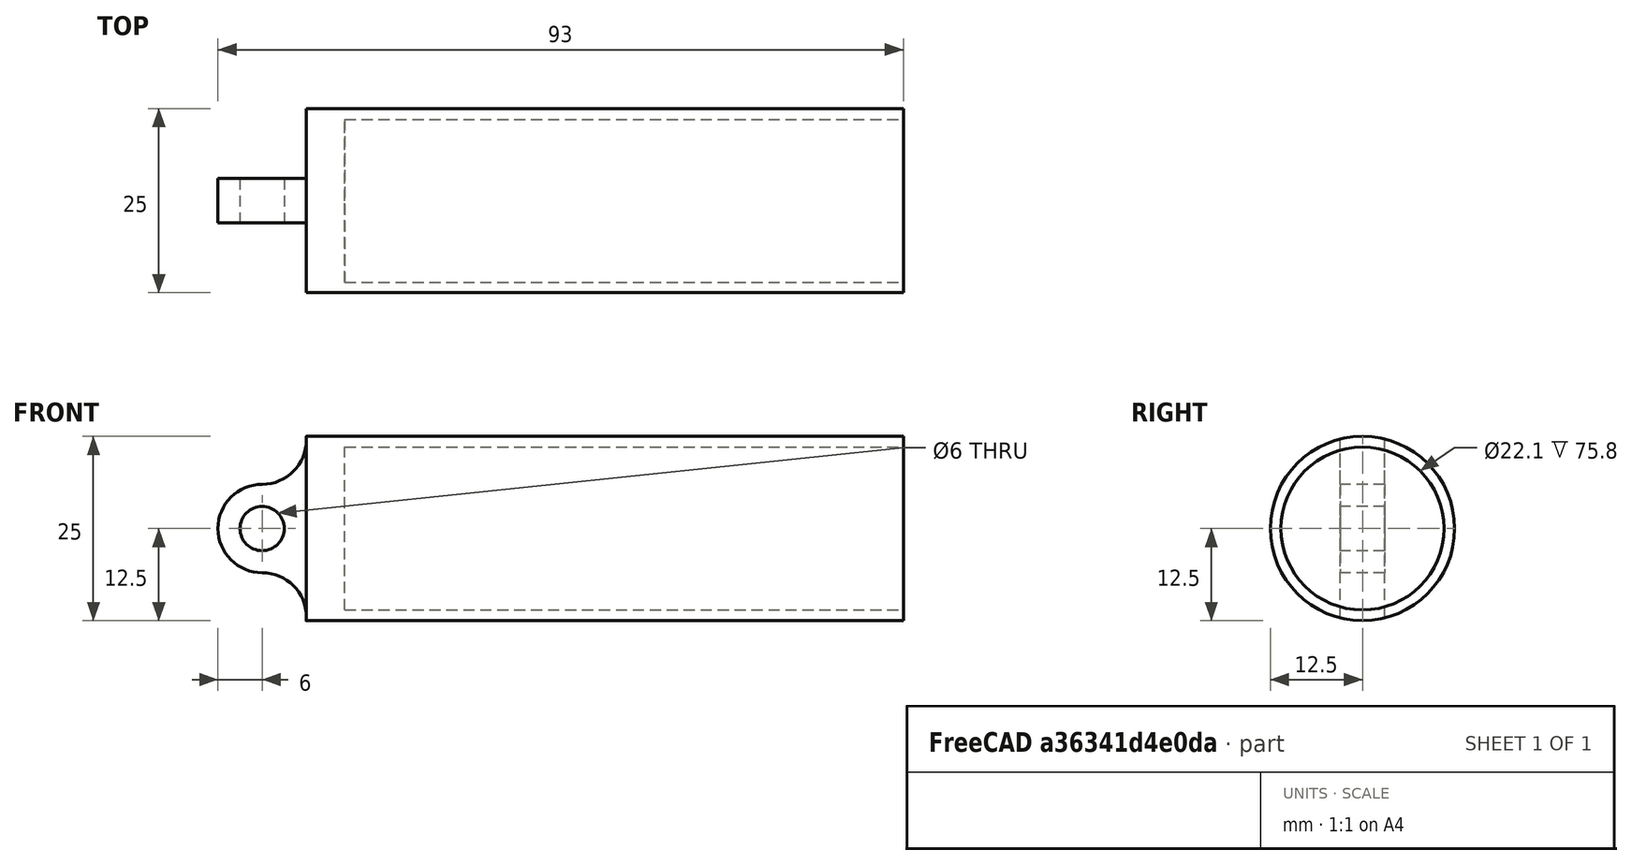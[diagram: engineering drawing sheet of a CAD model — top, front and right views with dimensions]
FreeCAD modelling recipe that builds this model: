
FCSTD DOCUMENT  (FreeCAD 0.17R13541 (Git))
Label: ERG-T-01-BC
License: All rights reserved
LicenseURL: http://en.wikipedia.org/wiki/All_rights_reserved
objects: Drawing::FeatureViewPython×25, Part::Cut×7, Part::Cylinder×6, Part::Box×4, Drawing::FeatureViewPart×3, Part::MultiFuse×1, Drawing::FeaturePage×1
note: 18 computed .brp shape members not serialized (recipe doc carries the construction recipe); baked Part::Feature solids carry a one-line shape summary decoded from their .brp

FEATURE [Part::Cylinder] Cylinder018  label="Cylinder016"
  Angle = 360
  AttacherType = Attacher::AttachEngine3D
  Height = 30
  Placement = pos=(-9,15,0) rot=(1,0,0;1.5708rad)
  Radius = 3
FEATURE [Part::Cylinder] Cylinder071  label="Cylinder076"
  Angle = 360
  AttacherType = Attacher::AttachEngine3D
  Height = 10
  Placement = pos=(-9,5,-12) rot=(1,0,0;1.5708rad)
  Radius = 6
FEATURE [Drawing::FeatureViewPython] dim164  # drawing view (typed FeaturePython)
  Rotation = 0
  ViewResult = <g> \n  <line x1="199.942305" y1="100.250000" x2="199.942305" y2="137.988628" style="stroke:rgb(255,0,0);stroke-width:0.10" />\n<line x1="78.411000" y1="100.250000" x2="78.411000" y2="137.988628" style="stroke:rgb(255,0,0);stroke-width:0.10" />\n<line x1="199.942305" y1="136.988628" x2="78.411000" y2="136.988628" style="stroke:rgb(255,0,0);stroke-width:0.10" /> \n  <polygon points="78.411000,136.988628 80.411000,137.488628 80.911000,136.988628 80.411000,136.488628" style="fill:rgb(255,0,0);stroke:rgb(255,0,0);stroke-width:0" /><polygon points="199.942305,136.988628 197.942305,136.488628 197.442305,136.988628 197.942305,137.488628" style="fill:rgb(255,0,0);stroke:rgb(255,0,0);stroke-width:0" /> \n  <text x="139.176652" y="134.988628" font-family="inherit" font-size="3.6" fill="rgb(0,0,0)" text-anchor="middle" transform="rotate(0.000000 139.176652,134.988628)" >81</text> </g>
  Visible = false
  X = 0
  Y = 0
  arrowL1 = 2
  arrowL2 = 0.5
  arrowW = 1
  arrow_scheme = 0
  autoPlaceOffset = 2
  autoPlaceText = true
  click1_x = 135.325
  click1_y = 136.989
  click2_x = 135.325
  click2_y = 136.989
  comma_decimal_place = false
  dimension_line_overshoot = 1
  gap_datum_points = 0
  halfDimension_linear = false
  lineColor = rgb(255,0,0)
  strokeWidth = 0.1
  textFormat_linear = %(value)3.1f
  textRenderer_color = rgb(0,0,0)
  textRenderer_family = inherit
  textRenderer_size = 3.6
  unit_custom_scale = 1
  unit_scheme = 0
FEATURE [Drawing::FeatureViewPython] dim170  # drawing view (typed FeaturePython)
  Rotation = 0
  ViewResult = <g> \n  <line x1="192.111000" y1="97.659500" x2="192.111000" y2="116.551430" style="stroke:rgb(255,0,0);stroke-width:0.10" />\n<line x1="199.942305" y1="100.250000" x2="199.942305" y2="116.551430" style="stroke:rgb(255,0,0);stroke-width:0.10" />\n<line x1="192.111000" y1="115.551430" x2="199.942305" y2="115.551430" style="stroke:rgb(255,0,0);stroke-width:0.10" /> \n  <polygon points="199.942305,115.551430 197.942305,115.051430 197.442305,115.551430 197.942305,116.051430" style="fill:rgb(255,0,0);stroke:rgb(255,0,0);stroke-width:0" /><polygon points="192.111000,115.551430 194.111000,116.051430 194.611000,115.551430 194.111000,115.051430" style="fill:rgb(255,0,0);stroke:rgb(255,0,0);stroke-width:0" /> \n  <text x="196.026653" y="113.551430" font-family="inherit" font-size="3.6" fill="rgb(0,0,0)" text-anchor="middle" transform="rotate(0.000000 196.026653,113.551430)" >  5</text> </g>
  Visible = false
  X = 0
  Y = 0
  arrowL1 = 2
  arrowL2 = 0.5
  arrowW = 1
  arrow_scheme = 0
  autoPlaceOffset = 2
  autoPlaceText = true
  click1_x = 199.481
  click1_y = 115.551
  click2_x = 199.481
  click2_y = 115.551
  comma_decimal_place = false
  dimension_line_overshoot = 1
  gap_datum_points = 0
  halfDimension_linear = false
  lineColor = rgb(255,0,0)
  strokeWidth = 0.1
  textFormat_linear = %(value)3.0f
  textRenderer_color = rgb(0,0,0)
  textRenderer_family = inherit
  textRenderer_size = 3.6
  unit_custom_scale = 1
  unit_scheme = 0
FEATURE [Drawing::FeatureViewPython] dim172  # drawing view (typed FeaturePython)
  Rotation = 0
  ViewResult = <g> \n  <line x1="208.911000" y1="63.500000" x2="208.911000" y2="43.465608" style="stroke:rgb(255,0,0);stroke-width:0.10" />\n<line x1="199.913265" y1="63.297950" x2="199.913265" y2="43.465608" style="stroke:rgb(255,0,0);stroke-width:0.10" />\n<line x1="208.911000" y1="44.465608" x2="199.913265" y2="44.465608" style="stroke:rgb(255,0,0);stroke-width:0.10" /> \n  <polygon points="199.913265,44.465608 201.913265,44.965608 202.413265,44.465608 201.913265,43.965608" style="fill:rgb(255,0,0);stroke:rgb(255,0,0);stroke-width:0" /><polygon points="208.911000,44.465608 206.911000,43.965608 206.411000,44.465608 206.911000,44.965608" style="fill:rgb(255,0,0);stroke:rgb(255,0,0);stroke-width:0" /> \n  <text x="204.412132" y="42.465608" font-family="inherit" font-size="3.6" fill="rgb(0,0,0)" text-anchor="middle" transform="rotate(0.000000 204.412132,42.465608)" >6</text> </g>
  Visible = false
  X = 0
  Y = 0
  arrowL1 = 2
  arrowL2 = 0.5
  arrowW = 1
  arrow_scheme = 0
  autoPlaceOffset = 2
  autoPlaceText = true
  click1_x = 203.94
  click1_y = 44.4656
  click2_x = 203.94
  click2_y = 44.4656
  comma_decimal_place = false
  dimension_line_overshoot = 1
  gap_datum_points = 0
  halfDimension_linear = false
  lineColor = rgb(255,0,0)
  strokeWidth = 0.1
  textFormat_linear = %(value)3.1f
  textRenderer_color = rgb(0,0,0)
  textRenderer_family = inherit
  textRenderer_size = 3.6
  unit_custom_scale = 1
  unit_scheme = 0
FEATURE [Drawing::FeatureViewPython] dim176  # drawing view (typed FeaturePython)
  Rotation = 0
  ViewResult = <g> \n  <line x1="208.911000" y1="63.500000" x2="232.243449" y2="63.500000" style="stroke:rgb(255,0,0);stroke-width:0.10" />\n<line x1="208.911000" y1="81.500000" x2="232.243449" y2="81.500000" style="stroke:rgb(255,0,0);stroke-width:0.10" />\n<line x1="231.243449" y1="63.500000" x2="231.243449" y2="81.500000" style="stroke:rgb(255,0,0);stroke-width:0.10" /> \n  <polygon points="231.243449,81.500000 231.743449,79.500000 231.243449,79.000000 230.743449,79.500000" style="fill:rgb(255,0,0);stroke:rgb(255,0,0);stroke-width:0" /><polygon points="231.243449,63.500000 230.743449,65.500000 231.243449,66.000000 231.743449,65.500000" style="fill:rgb(255,0,0);stroke:rgb(255,0,0);stroke-width:0" /> \n  <text x="229.243449" y="72.500000" font-family="inherit" font-size="3.6" fill="rgb(0,0,0)" text-anchor="middle" transform="rotate(-90.000000 229.243449,72.500000)" >12</text> </g>
  Visible = false
  X = 0
  Y = 0
  arrowL1 = 2
  arrowL2 = 0.5
  arrowW = 1
  arrow_scheme = 0
  autoPlaceOffset = 2
  autoPlaceText = true
  click1_x = 231.243
  click1_y = 82.2447
  click2_x = 231.243
  click2_y = 82.2447
  comma_decimal_place = false
  dimension_line_overshoot = 1
  gap_datum_points = 0
  halfDimension_linear = false
  lineColor = rgb(255,0,0)
  strokeWidth = 0.1
  textFormat_linear = %(value)3.3f
  textRenderer_color = rgb(0,0,0)
  textRenderer_family = inherit
  textRenderer_size = 3.6
  unit_custom_scale = 1
  unit_scheme = 0
FEATURE [Drawing::FeatureViewPython] dim177  # drawing view (typed FeaturePython)
  Rotation = 0
  ViewResult = <g> \n  <line x1="208.911000" y1="81.500000" x2="232.243449" y2="81.500000" style="stroke:rgb(255,0,0);stroke-width:0.10" />\n<line x1="208.911000" y1="99.500000" x2="232.243449" y2="99.500000" style="stroke:rgb(255,0,0);stroke-width:0.10" />\n<line x1="231.243449" y1="81.500000" x2="231.243449" y2="99.500000" style="stroke:rgb(255,0,0);stroke-width:0.10" /> \n  <polygon points="231.243449,99.500000 231.743449,97.500000 231.243449,97.000000 230.743449,97.500000" style="fill:rgb(255,0,0);stroke:rgb(255,0,0);stroke-width:0" /><polygon points="231.243449,81.500000 230.743449,83.500000 231.243449,84.000000 231.743449,83.500000" style="fill:rgb(255,0,0);stroke:rgb(255,0,0);stroke-width:0" /> \n  <text x="229.243449" y="90.500000" font-family="inherit" font-size="3.6" fill="rgb(0,0,0)" text-anchor="middle" transform="rotate(-90.000000 229.243449,90.500000)" >12</text> </g>
  Visible = false
  X = 0
  Y = 0
  arrowL1 = 2
  arrowL2 = 0.5
  arrowW = 1
  arrow_scheme = 0
  autoPlaceOffset = 2
  autoPlaceText = true
  click1_x = 231.243
  click1_y = 99.4068
  click2_x = 231.243
  click2_y = 99.4068
  comma_decimal_place = false
  dimension_line_overshoot = 1
  gap_datum_points = 0
  halfDimension_linear = false
  lineColor = rgb(255,0,0)
  strokeWidth = 0.1
  textFormat_linear = %(value)3.3f
  textRenderer_color = rgb(0,0,0)
  textRenderer_family = inherit
  textRenderer_size = 3.6
  unit_custom_scale = 1
  unit_scheme = 0
FEATURE [Drawing::FeatureViewPython] dim178  # drawing view (typed FeaturePython)
  Rotation = 0
  ViewResult = <g> \n  <line x1="208.911000" y1="99.500000" x2="232.243449" y2="99.500000" style="stroke:rgb(255,0,0);stroke-width:0.10" />\n<line x1="199.942305" y1="100.250000" x2="232.243449" y2="100.250000" style="stroke:rgb(255,0,0);stroke-width:0.10" />\n<line x1="231.243449" y1="99.500000" x2="231.243449" y2="100.250000" style="stroke:rgb(255,0,0);stroke-width:0.10" /> \n  <polygon points="231.243449,100.250000 230.743449,102.250000 231.243449,102.750000 231.743449,102.250000" style="fill:rgb(255,0,0);stroke:rgb(255,0,0);stroke-width:0" /><polygon points="231.243449,99.500000 231.743449,97.500000 231.243449,97.000000 230.743449,97.500000" style="fill:rgb(255,0,0);stroke:rgb(255,0,0);stroke-width:0" /> \n  <text x="229.243449" y="99.875000" font-family="inherit" font-size="3.6" fill="rgb(0,0,0)" text-anchor="middle" transform="rotate(-90.000000 229.243449,99.875000)" >0.5</text> </g>
  Visible = false
  X = 0
  Y = 0
  arrowL1 = 2
  arrowL2 = 0.5
  arrowW = 1
  arrow_scheme = 0
  autoPlaceOffset = 2
  autoPlaceText = true
  click1_x = 231.243
  click1_y = 99.7412
  click2_x = 231.243
  click2_y = 99.7412
  comma_decimal_place = false
  dimension_line_overshoot = 1
  gap_datum_points = 0
  halfDimension_linear = false
  lineColor = rgb(255,0,0)
  strokeWidth = 0.1
  textFormat_linear = %(value)3.3f
  textRenderer_color = rgb(0,0,0)
  textRenderer_family = inherit
  textRenderer_size = 3.6
  unit_custom_scale = 1
  unit_scheme = 0
FEATURE [Drawing::FeatureViewPython] dim179  # drawing view (typed FeaturePython)
  Rotation = 0
  ViewResult = <g> \n  <line x1="199.942305" y1="62.750000" x2="232.218157" y2="62.750000" style="stroke:rgb(255,0,0);stroke-width:0.10" />\n<line x1="208.911000" y1="63.500000" x2="232.218157" y2="63.500000" style="stroke:rgb(255,0,0);stroke-width:0.10" />\n<line x1="231.218157" y1="62.750000" x2="231.218157" y2="63.500000" style="stroke:rgb(255,0,0);stroke-width:0.10" /> \n  <polygon points="231.218157,63.500000 230.718157,65.500000 231.218157,66.000000 231.718157,65.500000" style="fill:rgb(255,0,0);stroke:rgb(255,0,0);stroke-width:0" /><polygon points="231.218157,62.750000 231.718157,60.750000 231.218157,60.250000 230.718157,60.750000" style="fill:rgb(255,0,0);stroke:rgb(255,0,0);stroke-width:0" /> \n  <text x="229.218157" y="63.125000" font-family="inherit" font-size="3.6" fill="rgb(0,0,0)" text-anchor="middle" transform="rotate(-90.000000 229.218157,63.125000)" >0.5</text> </g>
  Visible = false
  X = 0
  Y = 0
  arrowL1 = 2
  arrowL2 = 0.5
  arrowW = 1
  arrow_scheme = 0
  autoPlaceOffset = 2
  autoPlaceText = true
  click1_x = 231.218
  click1_y = 63.3591
  click2_x = 231.218
  click2_y = 63.3591
  comma_decimal_place = false
  dimension_line_overshoot = 1
  gap_datum_points = 0
  halfDimension_linear = false
  lineColor = rgb(255,0,0)
  strokeWidth = 0.1
  textFormat_linear = %(value)3.3f
  textRenderer_color = rgb(0,0,0)
  textRenderer_family = inherit
  textRenderer_size = 3.6
  unit_custom_scale = 1
  unit_scheme = 0
FEATURE [Drawing::FeatureViewPython] dia033  # drawing view (typed FeaturePython)
  Rotation = 0
  ViewResult = <g>  <circle cx ="208.911000" cy ="81.500000" r="0.250000" stroke="none" fill="rgb(255,0,0)" /> \n<line x1="192.329770" y1="55.807671" x2="211.351146" y2="85.280964" style="stroke:rgb(255,0,0);stroke-width:0.10" />\n<polygon points="206.470854,77.719036 207.135256,79.670592 207.826491,79.819572 207.975470,79.128337" style="fill:rgb(255,0,0);stroke:rgb(255,0,0);stroke-width:0" />\n<polygon points="211.351146,85.280964 210.686744,83.329408 209.995509,83.180428 209.846530,83.871663" style="fill:rgb(255,0,0);stroke:rgb(255,0,0);stroke-width:0" />\n<line x1="192.329770" y1="55.807671" x2="183.441881" y2="55.807671" style="stroke:rgb(255,0,0);stroke-width:0.10" />\n<text x="187.885826" y="53.807671" font-family="inherit" font-size="3.6" fill="rgb(0,0,0)" text-anchor="middle" transform="rotate(0.000000 187.885826,53.807671)" >Ø6</text> </g>
  Visible = false
  X = 0
  Y = 0
  arrowL1 = 2
  arrowL2 = 0.5
  arrowW = 1
  arrow_scheme = 0
  autoPlaceOffset = 2
  autoPlaceText = true
  centerPointDia = 0.5
  click1_x = 192.33
  click1_y = 55.8077
  click2_x = 183.442
  click2_y = 55.8077
  click3_x = 183.442
  click3_y = 55.8077
  comma_decimal_place = false
  lineColor = rgb(255,0,0)
  strokeWidth = 0.1
  textFormat_circular = Ø%(value)3.3f
  textRenderer_color = rgb(0,0,0)
  textRenderer_family = inherit
  textRenderer_size = 3.6
  unit_custom_scale = 1
  unit_scheme = 0
FEATURE [Drawing::FeatureViewPython] rad003  # drawing view (typed FeaturePython)
  Rotation = 0
  ViewResult = <g>  <circle cx ="208.911000" cy ="99.500000" r="0.250000" stroke="none" fill="rgb(255,0,0)" /> \n<line x1="205.552600" y1="94.422561" x2="208.911000" y2="99.500000" style="stroke:rgb(255,0,0);stroke-width:0.10" />\n<polygon points="203.945914,91.993474 204.632238,93.937429 205.325105,94.078620 205.466296,93.385753" style="fill:rgb(255,0,0);stroke:rgb(255,0,0);stroke-width:0" />\n<line x1="205.552600" y1="94.422561" x2="225.297800" y2="94.422561" style="stroke:rgb(255,0,0);stroke-width:0.10" />\n<text x="215.425200" y="93.422561" font-family="inherit" font-size="3.6" fill="rgb(0,0,0)" text-anchor="middle" transform="rotate(0.000000 215.425200,93.422561)" >R6</text> </g>
  Visible = false
  X = 0
  Y = 0
  arrowL1 = 2
  arrowL2 = 0.5
  arrowW = 1
  arrow_scheme = 0
  autoPlaceOffset = 1
  autoPlaceText = true
  centerPointDia = 0.5
  click1_x = 205.553
  click1_y = 94.4226
  click2_x = 225.298
  click2_y = 101.764
  click3_x = 225.298
  click3_y = 101.764
  comma_decimal_place = false
  lineColor = rgb(255,0,0)
  strokeWidth = 0.1
  textFormat_radial = R%(value)3.3f
  textRenderer_color = rgb(0,0,0)
  textRenderer_family = inherit
  textRenderer_size = 3.6
  unit_custom_scale = 1
  unit_scheme = 0
FEATURE [Part::Cylinder] Cylinder072  label="Cylinder077"
  Angle = 360
  AttacherType = Attacher::AttachEngine3D
  Height = 10
  Placement = pos=(-9,5,0) rot=(1,0,0;1.5708rad)
  Radius = 6
FEATURE [Drawing::FeatureViewPython] dim175  # drawing view (typed FeaturePython)
  Rotation = 0
  ViewResult = <g> \n  <line x1="78.411000" y1="64.925000" x2="70.243643" y2="64.925000" style="stroke:rgb(255,0,0);stroke-width:0.10" />\n<line x1="78.411000" y1="62.750000" x2="70.243643" y2="62.750000" style="stroke:rgb(255,0,0);stroke-width:0.10" />\n<line x1="71.243643" y1="64.925000" x2="71.243643" y2="62.750000" style="stroke:rgb(255,0,0);stroke-width:0.10" /> \n  <polygon points="71.243643,62.750000 71.743643,60.750000 71.243643,60.250000 70.743643,60.750000" style="fill:rgb(255,0,0);stroke:rgb(255,0,0);stroke-width:0" /><polygon points="71.243643,64.925000 70.743643,66.925000 71.243643,67.425000 71.743643,66.925000" style="fill:rgb(255,0,0);stroke:rgb(255,0,0);stroke-width:0" /> \n  <text x="69.243643" y="63.837500" font-family="inherit" font-size="3.6" fill="rgb(0,0,0)" text-anchor="middle" transform="rotate(-90.000000 69.243643,63.837500)" >1.45</text> </g>
  Visible = false
  X = 0
  Y = 0
  arrowL1 = 2
  arrowL2 = 0.5
  arrowW = 1
  arrow_scheme = 0
  autoPlaceOffset = 2
  autoPlaceText = true
  click1_x = 71.2436
  click1_y = 64.4174
  click2_x = 71.2436
  click2_y = 64.4174
  comma_decimal_place = false
  dimension_line_overshoot = 1
  gap_datum_points = 0
  halfDimension_linear = false
  lineColor = rgb(255,0,0)
  strokeWidth = 0.1
  textFormat_linear = %(value)3.3f
  textRenderer_color = rgb(0,0,0)
  textRenderer_family = inherit
  textRenderer_size = 3.6
  unit_custom_scale = 1.7
  unit_scheme = 0
FEATURE [Drawing::FeatureViewPython] dia031  # drawing view (typed FeaturePython)
  Rotation = 0
  ViewResult = <g>  <circle cx ="208.911000" cy ="81.500000" r="0.250000" stroke="none" fill="rgb(255,0,0)" /> \n<line x1="217.392661" y1="103.886283" x2="207.316648" y2="77.291908" style="stroke:rgb(255,0,0);stroke-width:0.10" />\n<polygon points="210.505352,85.708092 210.264317,83.660679 209.619601,83.370263 209.329185,84.014979" style="fill:rgb(255,0,0);stroke:rgb(255,0,0);stroke-width:0" />\n<polygon points="207.316648,77.291908 207.557683,79.339321 208.202399,79.629737 208.492815,78.985021" style="fill:rgb(255,0,0);stroke:rgb(255,0,0);stroke-width:0" />\n<line x1="217.392661" y1="103.886283" x2="224.970502" y2="103.886283" style="stroke:rgb(255,0,0);stroke-width:0.10" />\n<text x="221.181581" y="101.886283" font-family="inherit" font-size="3.6" fill="rgb(0,0,0)" text-anchor="middle" transform="rotate(0.000000 221.181581,101.886283)" >Ø6</text> </g>
  Visible = false
  X = 0
  Y = 0
  arrowL1 = 2
  arrowL2 = 0.5
  arrowW = 1
  arrow_scheme = 0
  autoPlaceOffset = 2
  autoPlaceText = true
  centerPointDia = 0.5
  click1_x = 217.393
  click1_y = 103.886
  click2_x = 224.971
  click2_y = 106.09
  click3_x = 224.971
  click3_y = 106.09
  comma_decimal_place = false
  lineColor = rgb(255,0,0)
  strokeWidth = 0.1
  textFormat_circular = Ø%(value)3.3f
  textRenderer_color = rgb(0,0,0)
  textRenderer_family = inherit
  textRenderer_size = 3.6
  unit_custom_scale = 1.7
  unit_scheme = 0
FEATURE [Drawing::FeatureViewPython] dim169  # drawing view (typed FeaturePython)
  Rotation = 0
  ViewResult = <g> \n  <line x1="257.295000" y1="72.500000" x2="286.142095" y2="72.500000" style="stroke:rgb(255,0,0);stroke-width:0.10" />\n<line x1="257.295000" y1="90.500000" x2="286.142095" y2="90.500000" style="stroke:rgb(255,0,0);stroke-width:0.10" />\n<line x1="285.142095" y1="72.500000" x2="285.142095" y2="90.500000" style="stroke:rgb(255,0,0);stroke-width:0.10" /> \n  <polygon points="285.142095,90.500000 285.642095,88.500000 285.142095,88.000000 284.642095,88.500000" style="fill:rgb(255,0,0);stroke:rgb(255,0,0);stroke-width:0" /><polygon points="285.142095,72.500000 284.642095,74.500000 285.142095,75.000000 285.642095,74.500000" style="fill:rgb(255,0,0);stroke:rgb(255,0,0);stroke-width:0" /> \n  <text x="283.142095" y="81.500000" font-family="inherit" font-size="3.6" fill="rgb(0,0,0)" text-anchor="middle" transform="rotate(-90.000000 283.142095,81.500000)" >12</text> </g>
  Visible = false
  X = 0
  Y = 0
  arrowL1 = 2
  arrowL2 = 0.5
  arrowW = 1
  arrow_scheme = 0
  autoPlaceOffset = 2
  autoPlaceText = true
  click1_x = 285.142
  click1_y = 88.4568
  click2_x = 285.142
  click2_y = 88.4568
  comma_decimal_place = false
  dimension_line_overshoot = 1
  gap_datum_points = 0
  halfDimension_linear = false
  lineColor = rgb(255,0,0)
  strokeWidth = 0.1
  textFormat_linear = %(value)3.3f
  textRenderer_color = rgb(0,0,0)
  textRenderer_family = inherit
  textRenderer_size = 3.6
  unit_custom_scale = 1.7
  unit_scheme = 0
FEATURE [Drawing::FeatureViewPython] dia029  # drawing view (typed FeaturePython)
  Rotation = 0
  ViewResult = <g>  <circle cx ="208.911000" cy ="81.500000" r="0.250000" stroke="none" fill="rgb(255,0,0)" /> \n<line x1="221.073512" y1="97.663424" x2="203.499633" y2="74.308539" style="stroke:rgb(255,0,0);stroke-width:0.10" />\n<polygon points="214.322367,88.691461 213.519367,86.792727 212.819210,86.693833 212.720316,87.393990" style="fill:rgb(255,0,0);stroke:rgb(255,0,0);stroke-width:0" />\n<polygon points="203.499633,74.308539 204.302633,76.207273 205.002790,76.306167 205.101684,75.606010" style="fill:rgb(255,0,0);stroke:rgb(255,0,0);stroke-width:0" />\n<line x1="221.073512" y1="97.663424" x2="229.903684" y2="97.663424" style="stroke:rgb(255,0,0);stroke-width:0.10" />\n<text x="225.488598" y="95.663424" font-family="inherit" font-size="3.6" fill="rgb(0,0,0)" text-anchor="middle" transform="rotate(0.000000 225.488598,95.663424)" >Ø12</text> </g>
  Visible = false
  X = 0
  Y = 0
  arrowL1 = 2
  arrowL2 = 0.5
  arrowW = 1
  arrow_scheme = 0
  autoPlaceOffset = 2
  autoPlaceText = true
  centerPointDia = 0.5
  click1_x = 221.074
  click1_y = 97.6634
  click2_x = 229.904
  click2_y = 101.394
  click3_x = 229.904
  click3_y = 101.394
  comma_decimal_place = false
  lineColor = rgb(255,0,0)
  strokeWidth = 0.1
  textFormat_circular = Ø%(value)3.3f
  textRenderer_color = rgb(0,0,0)
  textRenderer_family = inherit
  textRenderer_size = 3.6
  unit_custom_scale = 1.7
  unit_scheme = 0
FEATURE [Drawing::FeatureViewPython] dia032  # drawing view (typed FeaturePython)
  Rotation = 0
  ViewResult = <g>  <circle cx ="208.911000" cy ="63.500000" r="0.250000" stroke="none" fill="rgb(255,0,0)" /> \n<line x1="218.955339" y1="44.484330" x2="204.707459" y2="71.458030" style="stroke:rgb(255,0,0);stroke-width:0.10" />\n<polygon points="213.114541,55.541970 211.738308,57.076891 211.946891,57.752534 212.622534,57.543951" style="fill:rgb(255,0,0);stroke:rgb(255,0,0);stroke-width:0" />\n<polygon points="204.707459,71.458030 206.083692,69.923109 205.875109,69.247466 205.199466,69.456049" style="fill:rgb(255,0,0);stroke:rgb(255,0,0);stroke-width:0" />\n<line x1="218.955339" y1="44.484330" x2="230.317138" y2="44.484330" style="stroke:rgb(255,0,0);stroke-width:0.10" />\n<text x="224.636239" y="42.484330" font-family="inherit" font-size="3.6" fill="rgb(0,0,0)" text-anchor="middle" transform="rotate(0.000000 224.636239,42.484330)" >Ø12</text> </g>
  Visible = false
  X = 0
  Y = 0
  arrowL1 = 2
  arrowL2 = 0.5
  arrowW = 1
  arrow_scheme = 0
  autoPlaceOffset = 2
  autoPlaceText = true
  centerPointDia = 0.5
  click1_x = 218.955
  click1_y = 44.4843
  click2_x = 230.317
  click2_y = 45.2546
  click3_x = 230.317
  click3_y = 45.2546
  comma_decimal_place = false
  lineColor = rgb(255,0,0)
  strokeWidth = 0.1
  textFormat_circular = Ø%(value)3.3f
  textRenderer_color = rgb(0,0,0)
  textRenderer_family = inherit
  textRenderer_size = 3.6
  unit_custom_scale = 1.7
  unit_scheme = 0
FEATURE [Drawing::FeatureViewPython] rad001  # drawing view (typed FeaturePython)
  Rotation = 0
  ViewResult = <g>  <circle cx ="208.911000" cy ="63.500000" r="0.250000" stroke="none" fill="rgb(255,0,0)" /> \n<line x1="206.226171" y1="68.633374" x2="208.911000" y2="63.500000" style="stroke:rgb(255,0,0);stroke-width:0.10" />\n<polygon points="204.739914,71.475089 206.109882,69.934574 205.898549,69.259786 205.223761,69.471120" style="fill:rgb(255,0,0);stroke:rgb(255,0,0);stroke-width:0" />\n<line x1="206.226171" y1="68.633374" x2="218.289995" y2="68.633374" style="stroke:rgb(255,0,0);stroke-width:0.10" />\n<text x="212.258083" y="67.633374" font-family="inherit" font-size="3.6" fill="rgb(0,0,0)" text-anchor="middle" transform="rotate(0.000000 212.258083,67.633374)" >R6</text> </g>
  Visible = false
  X = 0
  Y = 0
  arrowL1 = 2
  arrowL2 = 0.5
  arrowW = 1
  arrow_scheme = 0
  autoPlaceOffset = 1
  autoPlaceText = true
  centerPointDia = 0.5
  click1_x = 206.226
  click1_y = 68.6334
  click2_x = 218.29
  click2_y = 68.3073
  click3_x = 218.29
  click3_y = 68.3073
  comma_decimal_place = false
  lineColor = rgb(255,0,0)
  strokeWidth = 0.1
  textFormat_radial = R%(value)3.3f
  textRenderer_color = rgb(0,0,0)
  textRenderer_family = inherit
  textRenderer_size = 3.6
  unit_custom_scale = 1.7
  unit_scheme = 0
FEATURE [Drawing::FeatureViewPython] rad002  # drawing view (typed FeaturePython)
  Rotation = 0
  ViewResult = <g>  <circle cx ="208.911000" cy ="81.500000" r="0.250000" stroke="none" fill="rgb(255,0,0)" /> \n<line x1="212.747157" y1="74.502261" x2="208.911000" y2="81.500000" style="stroke:rgb(255,0,0);stroke-width:0.10" />\n<polygon points="213.237355,73.608064 211.837502,75.121475 212.035590,75.800269 212.714384,75.602181" style="fill:rgb(255,0,0);stroke:rgb(255,0,0);stroke-width:0" />\n<line x1="212.747157" y1="74.502261" x2="224.810981" y2="74.502261" style="stroke:rgb(255,0,0);stroke-width:0.10" />\n<text x="218.779069" y="73.502261" font-family="inherit" font-size="3.6" fill="rgb(0,0,0)" text-anchor="middle" transform="rotate(0.000000 218.779069,73.502261)" >R6</text> </g>
  Visible = false
  X = 0
  Y = 0
  arrowL1 = 2
  arrowL2 = 0.5
  arrowW = 1
  arrow_scheme = 0
  autoPlaceOffset = 1
  autoPlaceText = true
  centerPointDia = 0.5
  click1_x = 212.747
  click1_y = 74.5023
  click2_x = 224.811
  click2_y = 77.5997
  click3_x = 224.811
  click3_y = 77.5997
  comma_decimal_place = false
  lineColor = rgb(255,0,0)
  strokeWidth = 0.1
  textFormat_radial = R%(value)3.3f
  textRenderer_color = rgb(0,0,0)
  textRenderer_family = inherit
  textRenderer_size = 3.6
  unit_custom_scale = 1.7
  unit_scheme = 0
FEATURE [Part::Cylinder] Cylinder006  label="Cylinder004"
  Angle = 360
  AttacherType = Attacher::AttachEngine3D
  Height = 75.8
  Placement = pos=(2.2,0,0) rot=(0,1,0;1.5708rad)
  Radius = 11.05
FEATURE [Part::Cylinder] Cylinder070  label="Cylinder075"
  Angle = 360
  AttacherType = Attacher::AttachEngine3D
  Height = 10
  Placement = pos=(-9,5,12) rot=(1,0,0;1.5708rad)
  Radius = 6
FEATURE [Part::Box] Box003  label="Cube003"
  AttacherType = Attacher::AttachEngine3D
  Height = 38
  Length = 6
  Placement = pos=(-9,-5,-19) rot=(0,0,1;0rad)
  Width = 10
FEATURE [Drawing::FeatureViewPython] dia030  # drawing view (typed FeaturePython)
  Rotation = 0
  ViewResult = <g>  <circle cx ="44.205300" cy ="81.500000" r="0.250000" stroke="none" fill="rgb(255,0,0)" /> \n<line x1="25.227044" y1="116.121433" x2="52.172618" y2="66.965473" style="stroke:rgb(255,0,0);stroke-width:0.10" />\n<polygon points="36.237982,96.034527 37.637795,94.521079 37.439689,93.842290 36.760900,94.040396" style="fill:rgb(255,0,0);stroke:rgb(255,0,0);stroke-width:0" />\n<polygon points="52.172618,66.965473 50.772805,68.478921 50.970911,69.157710 51.649700,68.959604" style="fill:rgb(255,0,0);stroke:rgb(255,0,0);stroke-width:0" />\n<line x1="25.227044" y1="116.121433" x2="13.865246" y2="116.121433" style="stroke:rgb(255,0,0);stroke-width:0.10" />\n<text x="19.546145" y="114.121433" font-family="inherit" font-size="3.6" fill="rgb(0,0,0)" text-anchor="middle" transform="rotate(0.000000 19.546145,114.121433)" >Ø22.1</text> </g>
  Visible = false
  X = 0
  Y = 0
  arrowL1 = 2
  arrowL2 = 0.5
  arrowW = 1
  arrow_scheme = 0
  autoPlaceOffset = 2
  autoPlaceText = true
  centerPointDia = 0.5
  click1_x = 25.227
  click1_y = 116.121
  click2_x = 13.8652
  click2_y = 117.469
  click3_x = 13.8652
  click3_y = 117.469
  comma_decimal_place = false
  lineColor = rgb(255,0,0)
  strokeWidth = 0.1
  textFormat_circular = Ø%(value)3.3f
  textRenderer_color = rgb(0,0,0)
  textRenderer_family = inherit
  textRenderer_size = 3.6
  unit_custom_scale = 1.7
  unit_scheme = 0
FEATURE [Drawing::FeatureViewPython] dim165  # drawing view (typed FeaturePython)
  Rotation = 0
  ViewResult = <g> \n  <line x1="192.111000" y1="98.075000" x2="192.111000" y2="126.653790" style="stroke:rgb(255,0,0);stroke-width:0.10" />\n<line x1="78.411000" y1="98.075000" x2="78.411000" y2="126.653790" style="stroke:rgb(255,0,0);stroke-width:0.10" />\n<line x1="192.111000" y1="125.653790" x2="78.411000" y2="125.653790" style="stroke:rgb(255,0,0);stroke-width:0.10" /> \n  <polygon points="78.411000,125.653790 80.411000,126.153790 80.911000,125.653790 80.411000,125.153790" style="fill:rgb(255,0,0);stroke:rgb(255,0,0);stroke-width:0" /><polygon points="192.111000,125.653790 190.111000,125.153790 189.611000,125.653790 190.111000,126.153790" style="fill:rgb(255,0,0);stroke:rgb(255,0,0);stroke-width:0" /> \n  <text x="135.261000" y="123.653790" font-family="inherit" font-size="3.6" fill="rgb(0,0,0)" text-anchor="middle" transform="rotate(0.000000 135.261000,123.653790)" >75.8</text> </g>
  Visible = false
  X = 0
  Y = 0
  arrowL1 = 2
  arrowL2 = 0.5
  arrowW = 1
  arrow_scheme = 0
  autoPlaceOffset = 2
  autoPlaceText = true
  click1_x = 141.926
  click1_y = 125.654
  click2_x = 141.926
  click2_y = 125.654
  comma_decimal_place = false
  dimension_line_overshoot = 1
  gap_datum_points = 0
  halfDimension_linear = false
  lineColor = rgb(255,0,0)
  strokeWidth = 0.1
  textFormat_linear = %(value)3.3f
  textRenderer_color = rgb(0,0,0)
  textRenderer_family = inherit
  textRenderer_size = 3.6
  unit_custom_scale = 1.7
  unit_scheme = 0
FEATURE [Drawing::FeatureViewPython] dim166  # drawing view (typed FeaturePython)
  Rotation = 0
  ViewResult = <g> \n  <line x1="192.111000" y1="64.925000" x2="187.498557" y2="64.925000" style="stroke:rgb(255,0,0);stroke-width:0.10" />\n<line x1="192.111000" y1="98.075000" x2="187.498557" y2="98.075000" style="stroke:rgb(255,0,0);stroke-width:0.10" />\n<line x1="188.498557" y1="64.925000" x2="188.498557" y2="98.075000" style="stroke:rgb(255,0,0);stroke-width:0.10" /> \n  <polygon points="188.498557,98.075000 188.998557,96.075000 188.498557,95.575000 187.998557,96.075000" style="fill:rgb(255,0,0);stroke:rgb(255,0,0);stroke-width:0" /><polygon points="188.498557,64.925000 187.998557,66.925000 188.498557,67.425000 188.998557,66.925000" style="fill:rgb(255,0,0);stroke:rgb(255,0,0);stroke-width:0" /> \n  <text x="186.498557" y="81.500000" font-family="inherit" font-size="3.6" fill="rgb(0,0,0)" text-anchor="middle" transform="rotate(-90.000000 186.498557,81.500000)" >22.1</text> </g>
  Visible = false
  X = 0
  Y = 0
  arrowL1 = 2
  arrowL2 = 0.5
  arrowW = 1
  arrow_scheme = 0
  autoPlaceOffset = 2
  autoPlaceText = true
  click1_x = 188.499
  click1_y = 97.4939
  click2_x = 188.499
  click2_y = 97.4939
  comma_decimal_place = false
  dimension_line_overshoot = 1
  gap_datum_points = 0
  halfDimension_linear = false
  lineColor = rgb(255,0,0)
  strokeWidth = 0.1
  textFormat_linear = %(value)3.3f
  textRenderer_color = rgb(0,0,0)
  textRenderer_family = inherit
  textRenderer_size = 3.6
  unit_custom_scale = 1.7
  unit_scheme = 0
FEATURE [Drawing::FeatureViewPython] dim167  # drawing view (typed FeaturePython)
  Rotation = 0
  ViewResult = <g> \n  <line x1="199.942305" y1="62.750000" x2="176.484655" y2="62.750000" style="stroke:rgb(255,0,0);stroke-width:0.10" />\n<line x1="199.942305" y1="100.250000" x2="176.484655" y2="100.250000" style="stroke:rgb(255,0,0);stroke-width:0.10" />\n<line x1="177.484655" y1="62.750000" x2="177.484655" y2="100.250000" style="stroke:rgb(255,0,0);stroke-width:0.10" /> \n  <polygon points="177.484655,100.250000 177.984655,98.250000 177.484655,97.750000 176.984655,98.250000" style="fill:rgb(255,0,0);stroke:rgb(255,0,0);stroke-width:0" /><polygon points="177.484655,62.750000 176.984655,64.750000 177.484655,65.250000 177.984655,64.750000" style="fill:rgb(255,0,0);stroke:rgb(255,0,0);stroke-width:0" /> \n  <text x="175.484655" y="81.500000" font-family="inherit" font-size="3.6" fill="rgb(0,0,0)" text-anchor="middle" transform="rotate(-90.000000 175.484655,81.500000)" >25</text> </g>
  Visible = false
  X = 0
  Y = 0
  arrowL1 = 2
  arrowL2 = 0.5
  arrowW = 1
  arrow_scheme = 0
  autoPlaceOffset = 2
  autoPlaceText = true
  click1_x = 177.485
  click1_y = 101.262
  click2_x = 177.485
  click2_y = 101.262
  comma_decimal_place = false
  dimension_line_overshoot = 1
  gap_datum_points = 0
  halfDimension_linear = false
  lineColor = rgb(255,0,0)
  strokeWidth = 0.1
  textFormat_linear = %(value)3.3f
  textRenderer_color = rgb(0,0,0)
  textRenderer_family = inherit
  textRenderer_size = 3.6
  unit_custom_scale = 1.7
  unit_scheme = 0
FEATURE [Drawing::FeatureViewPython] dim168  # drawing view (typed FeaturePython)
  Rotation = 0
  ViewResult = <g> \n  <line x1="208.911000" y1="81.500000" x2="208.911000" y2="116.544202" style="stroke:rgb(255,0,0);stroke-width:0.10" />\n<line x1="199.911000" y1="81.500000" x2="199.911000" y2="116.544202" style="stroke:rgb(255,0,0);stroke-width:0.10" />\n<line x1="208.911000" y1="115.544202" x2="199.911000" y2="115.544202" style="stroke:rgb(255,0,0);stroke-width:0.10" /> \n  <polygon points="199.911000,115.544202 201.911000,116.044202 202.411000,115.544202 201.911000,115.044202" style="fill:rgb(255,0,0);stroke:rgb(255,0,0);stroke-width:0" /><polygon points="208.911000,115.544202 206.911000,115.044202 206.411000,115.544202 206.911000,116.044202" style="fill:rgb(255,0,0);stroke:rgb(255,0,0);stroke-width:0" /> \n  <text x="204.411000" y="113.544202" font-family="inherit" font-size="3.6" fill="rgb(0,0,0)" text-anchor="middle" transform="rotate(0.000000 204.411000,113.544202)" >6</text> </g>
  Visible = false
  X = 0
  Y = 0
  arrowL1 = 2
  arrowL2 = 0.5
  arrowW = 1
  arrow_scheme = 0
  autoPlaceOffset = 2
  autoPlaceText = true
  click1_x = 202.645
  click1_y = 115.544
  click2_x = 202.645
  click2_y = 115.544
  comma_decimal_place = false
  dimension_line_overshoot = 1
  gap_datum_points = 0
  halfDimension_linear = false
  lineColor = rgb(255,0,0)
  strokeWidth = 0.1
  textFormat_linear = %(value)3.3f
  textRenderer_color = rgb(0,0,0)
  textRenderer_family = inherit
  textRenderer_size = 3.6
  unit_custom_scale = 1.7
  unit_scheme = 0
FEATURE [Drawing::FeatureViewPython] dim171  # drawing view (typed FeaturePython)
  Rotation = 0
  ViewResult = <g> \n  <line x1="248.295000" y1="99.702050" x2="248.295000" y2="114.036371" style="stroke:rgb(255,0,0);stroke-width:0.10" />\n<line x1="257.295000" y1="99.702050" x2="257.295000" y2="114.036371" style="stroke:rgb(255,0,0);stroke-width:0.10" />\n<line x1="248.295000" y1="113.036371" x2="257.295000" y2="113.036371" style="stroke:rgb(255,0,0);stroke-width:0.10" /> \n  <polygon points="257.295000,113.036371 255.295000,112.536371 254.795000,113.036371 255.295000,113.536371" style="fill:rgb(255,0,0);stroke:rgb(255,0,0);stroke-width:0" /><polygon points="248.295000,113.036371 250.295000,113.536371 250.795000,113.036371 250.295000,112.536371" style="fill:rgb(255,0,0);stroke:rgb(255,0,0);stroke-width:0" /> \n  <text x="252.795000" y="111.036371" font-family="inherit" font-size="3.6" fill="rgb(0,0,0)" text-anchor="middle" transform="rotate(0.000000 252.795000,111.036371)" >6</text> </g>
  Visible = false
  X = 0
  Y = 0
  arrowL1 = 2
  arrowL2 = 0.5
  arrowW = 1
  arrow_scheme = 0
  autoPlaceOffset = 2
  autoPlaceText = true
  click1_x = 258.225
  click1_y = 113.036
  click2_x = 258.225
  click2_y = 113.036
  comma_decimal_place = false
  dimension_line_overshoot = 1
  gap_datum_points = 0
  halfDimension_linear = false
  lineColor = rgb(255,0,0)
  strokeWidth = 0.1
  textFormat_linear = %(value)3.3f
  textRenderer_color = rgb(0,0,0)
  textRenderer_family = inherit
  textRenderer_size = 3.6
  unit_custom_scale = 1.7
  unit_scheme = 0
FEATURE [Drawing::FeatureViewPython] dim173  # drawing view (typed FeaturePython)
  Rotation = 0
  ViewResult = <g> \n  <line x1="257.295000" y1="77.000000" x2="279.929026" y2="77.000000" style="stroke:rgb(255,0,0);stroke-width:0.10" />\n<line x1="257.295000" y1="86.000000" x2="279.929026" y2="86.000000" style="stroke:rgb(255,0,0);stroke-width:0.10" />\n<line x1="278.929026" y1="77.000000" x2="278.929026" y2="86.000000" style="stroke:rgb(255,0,0);stroke-width:0.10" /> \n  <polygon points="278.929026,86.000000 279.429026,84.000000 278.929026,83.500000 278.429026,84.000000" style="fill:rgb(255,0,0);stroke:rgb(255,0,0);stroke-width:0" /><polygon points="278.929026,77.000000 278.429026,79.000000 278.929026,79.500000 279.429026,79.000000" style="fill:rgb(255,0,0);stroke:rgb(255,0,0);stroke-width:0" /> \n  <text x="276.929026" y="81.500000" font-family="inherit" font-size="3.6" fill="rgb(0,0,0)" text-anchor="middle" transform="rotate(-90.000000 276.929026,81.500000)" >6</text> </g>
  Visible = false
  X = 0
  Y = 0
  arrowL1 = 2
  arrowL2 = 0.5
  arrowW = 1
  arrow_scheme = 0
  autoPlaceOffset = 2
  autoPlaceText = true
  click1_x = 278.929
  click1_y = 84.7428
  click2_x = 278.929
  click2_y = 84.7428
  comma_decimal_place = false
  dimension_line_overshoot = 1
  gap_datum_points = 0
  halfDimension_linear = false
  lineColor = rgb(255,0,0)
  strokeWidth = 0.1
  textFormat_linear = %(value)3.3f
  textRenderer_color = rgb(0,0,0)
  textRenderer_family = inherit
  textRenderer_size = 3.6
  unit_custom_scale = 1.7
  unit_scheme = 0
FEATURE [Drawing::FeatureViewPython] dim174  # drawing view (typed FeaturePython)
  Rotation = 0
  ViewResult = <g> \n  <line x1="78.411000" y1="98.075000" x2="71.178333" y2="98.075000" style="stroke:rgb(255,0,0);stroke-width:0.10" />\n<line x1="78.411000" y1="100.250000" x2="71.178333" y2="100.250000" style="stroke:rgb(255,0,0);stroke-width:0.10" />\n<line x1="72.178333" y1="98.075000" x2="72.178333" y2="100.250000" style="stroke:rgb(255,0,0);stroke-width:0.10" /> \n  <polygon points="72.178333,100.250000 71.678333,102.250000 72.178333,102.750000 72.678333,102.250000" style="fill:rgb(255,0,0);stroke:rgb(255,0,0);stroke-width:0" /><polygon points="72.178333,98.075000 72.678333,96.075000 72.178333,95.575000 71.678333,96.075000" style="fill:rgb(255,0,0);stroke:rgb(255,0,0);stroke-width:0" /> \n  <text x="70.178333" y="99.162500" font-family="inherit" font-size="3.6" fill="rgb(0,0,0)" text-anchor="middle" transform="rotate(-90.000000 70.178333,99.162500)" >1.45</text> </g>
  Visible = false
  X = 0
  Y = 0
  arrowL1 = 2
  arrowL2 = 0.5
  arrowW = 1
  arrow_scheme = 0
  autoPlaceOffset = 2
  autoPlaceText = true
  click1_x = 72.1783
  click1_y = 98.8022
  click2_x = 72.1783
  click2_y = 98.8022
  comma_decimal_place = false
  dimension_line_overshoot = 1
  gap_datum_points = 0
  halfDimension_linear = false
  lineColor = rgb(255,0,0)
  strokeWidth = 0.1
  textFormat_linear = %(value)3.3f
  textRenderer_color = rgb(0,0,0)
  textRenderer_family = inherit
  textRenderer_size = 3.6
  unit_custom_scale = 1.7
  unit_scheme = 0
FEATURE [Part::Box] Box002  label="Cube002"
  AttacherType = Attacher::AttachEngine3D
  Height = 38
  Length = 14
  Placement = pos=(-17,-5,-19) rot=(0,0,1;0rad)
  Width = 10
FEATURE [Drawing::FeatureViewPython] dia028  # drawing view (typed FeaturePython)
  Rotation = 0
  ViewResult = <g>  <circle cx ="44.205300" cy ="81.500000" r="0.250000" stroke="none" fill="rgb(255,0,0)" /> \n<line x1="22.338451" y1="39.477436" x2="51.856384" y2="96.203453" style="stroke:rgb(255,0,0);stroke-width:0.10" />\n<polygon points="36.554216,66.796547 37.033880,68.801521 37.708225,69.014262 37.920967,68.339917" style="fill:rgb(255,0,0);stroke:rgb(255,0,0);stroke-width:0" />\n<polygon points="51.856384,96.203453 51.376720,94.198479 50.702375,93.985738 50.489633,94.660083" style="fill:rgb(255,0,0);stroke:rgb(255,0,0);stroke-width:0" />\n<line x1="22.338451" y1="39.477436" x2="12.902381" y2="39.477436" style="stroke:rgb(255,0,0);stroke-width:0.10" />\n<text x="17.620416" y="37.477436" font-family="inherit" font-size="3.6" fill="rgb(0,0,0)" text-anchor="middle" transform="rotate(0.000000 17.620416,37.477436)" >Ø22.1</text> </g>
  Visible = false
  X = 0
  Y = 0
  arrowL1 = 2
  arrowL2 = 0.5
  arrowW = 1
  arrow_scheme = 0
  autoPlaceOffset = 2
  autoPlaceText = true
  centerPointDia = 0.5
  click1_x = 22.3385
  click1_y = 39.4774
  click2_x = 12.9024
  click2_y = 37.7443
  click3_x = 12.9024
  click3_y = 37.7443
  comma_decimal_place = false
  lineColor = rgb(255,0,0)
  strokeWidth = 0.1
  textFormat_circular = Ø%(value)3.3f
  textRenderer_color = rgb(0,0,0)
  textRenderer_family = inherit
  textRenderer_size = 3.6
  unit_custom_scale = 1.7
  unit_scheme = 0
FEATURE [Part::Box] Box001  label="Cube001"
  AttacherType = Attacher::AttachEngine3D
  Height = 30
  Length = 14
  Placement = pos=(-17,-18,-15) rot=(0,0,1;0rad)
  Width = 15
FEATURE [Part::Cylinder] Cylinder005  label="Cylinder003"
  Angle = 360
  AttacherType = Attacher::AttachEngine3D
  Height = 95
  Placement = pos=(-17,0,0) rot=(0,1,0;1.5708rad)
  Radius = 12.5
FEATURE [Part::Cut] Cut064
  Base = -> Box002
  Tool = -> Box003
FEATURE [Part::Cut] Cut065
  Base = -> Cut064
  Tool = -> Cylinder072
FEATURE [Part::MultiFuse] Fusion015
  Shapes = -> [Cylinder070,Cylinder071,Cut065]
FEATURE [Part::Box] Box  label="Cube"
  AttacherType = Attacher::AttachEngine3D
  Height = 30
  Length = 14
  Placement = pos=(-17,3,-15) rot=(0,0,1;0rad)
  Width = 15
FEATURE [Part::Cut] Cut010
  Base = -> Cylinder005
  Tool = -> Box
FEATURE [Part::Cut] Cut011
  Base = -> Cut010
  Tool = -> Box001
FEATURE [Part::Cut] Cut012
  Base = -> Cut011
  Tool = -> Cylinder018
FEATURE [Part::Cut] Cut013  label="BatteryCapHole"
  Base = -> Cut012
  Tool = -> Cylinder006
FEATURE [Part::Cut] Cut066  label="BatteryCap2"
  Base = -> Cut013
  Tool = -> Fusion015
FEATURE [Drawing::FeatureViewPart] Ortho023  label="Ortho_0_011"
  Direction = (1,0,0)
  HiddenWidth = 0.15
  LineWidth = 0.35
  Rotation = -90
  Scale = 1.5
  ShowHiddenLines = false
  ShowSmoothLines = false
  Source = -> Cut066
  Tolerance = 0.05
  ViewResult = <g id="Ortho_0_011"\n   transform="rotate(-90,44.2053,81.5) translate(44.2053,81.5) scale(1.5,1.5)"\n  >\n<g   fill="none"\n   stroke="rgb(0, 0, 0)"\n   stroke-linecap="butt"\n   stroke-linejoin="miter"\n   stroke-width="0.233333"\n   transform="scale(1,-1)"\n  >\n<circle cx ="2.10942e-14" cy ="0" r ="12.5" /><circle cx ="1.6831e-14" cy ="0" r ="11.05" /></g>\n</g>
  Visible = false
  X = 44.2053
  Y = 81.5
FEATURE [Drawing::FeatureViewPart] Ortho024  label="Ortho_1_006"
  Direction = (0,1,0)
  HiddenWidth = 0.15
  LineWidth = 0.35
  Rotation = -90
  Scale = 1.5
  ShowHiddenLines = true
  ShowSmoothLines = false
  Source = -> Cut066
  Tolerance = 0.05
  ViewResult = <blob: 4195 chars omitted>
  Visible = false
  X = 195.411
  Y = 81.5
FEATURE [Drawing::FeatureViewPart] Ortho025  label="Ortho_2_002"
  Direction = (-1,0,0)
  HiddenWidth = 0.15
  LineWidth = 0.35
  Rotation = 90
  Scale = 1.5
  ShowHiddenLines = true
  ShowSmoothLines = false
  Source = -> Cut066
  Tolerance = 0.05
  ViewResult = <blob: 4577 chars omitted>
  Visible = false
  X = 252.795
  Y = 81.5
FEATURE [Drawing::FeaturePage] Page010  label="BatteryCap2-SV"
  EditableTexts = Dr. Zoidberg | 05.02.2019 | x1.0 | unknown | ERG-T-01 | Battery Cap. Side View. | 05 | 06
  Group = -> [Ortho023,Ortho024,Ortho025,dia028,dia030,dim165,dim166,dim167,dia029,dim168,dim171,dim173,dim174,dim175,dia031,dia032,dim169,rad001,rad002,dim164,dim170,dim172,dim176,dim177,dim178,dim179,dia033,rad003]
  Template = <path>//share/freecad/Mod/Drawing/Templates/A4_Landscape.svg
note: 1 file-system path scrubbed to <path> (originals preserved in the JSON sidecar)
